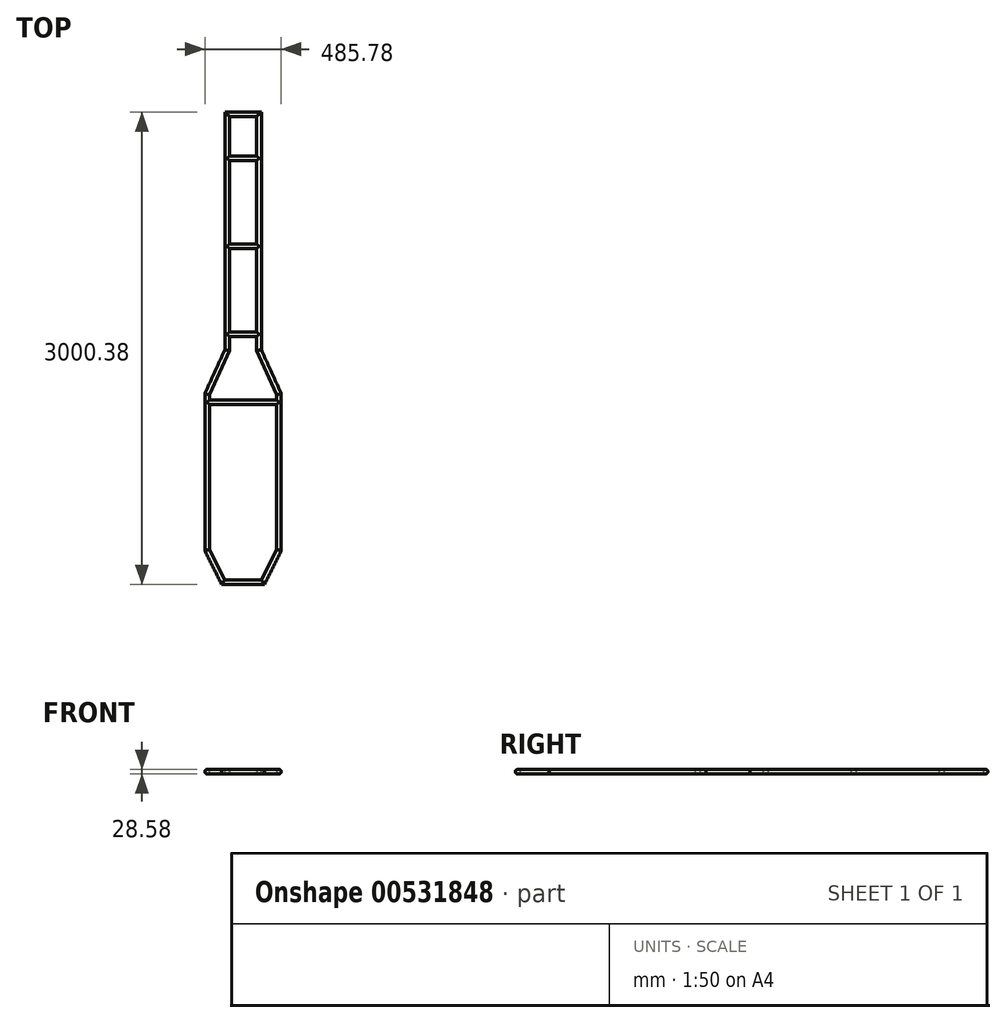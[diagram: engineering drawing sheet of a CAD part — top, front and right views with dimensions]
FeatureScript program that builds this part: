
annotation { "Feature Type Name" : "Feature", "Feature Type Description" : "" }
export const myFeature = defineFeature(function(context is Context, id is Id, definition is map)
    precondition{}
    {
        {
            var Q0;
            Q0=qCreatedBy(makeId("Top.planeOp"),FACE);
            var sketch = newSketch(context, id + "F0", { "sketchPlane" : qUnion([Q0])});
            skLineSegment(sketch, "E0", {"start": v(-228.6, 495.3) * mm, "end": v(-228.6, -495.3) * mm});
            skLineSegment(sketch, "E1", {"start": v(228.6, 495.3) * mm, "end": v(228.6, -495.3) * mm});
            skLineSegment(sketch, "E2", {"start": v(-228.6, 0) * mm, "end": v(228.6, 0) * mm, "construction": true});
            skLineSegment(sketch, "E3", {"start": v(-228.6, 292.1) * mm, "end": v(228.6, 101.6) * mm, "construction": true});
            skLineSegment(sketch, "E4", {"start": v(228.6, 292.1) * mm, "end": v(-228.6, 101.6) * mm, "construction": true});
            skLineSegment(sketch, "E5", {"start": v(-228.6, -292.1) * mm, "end": v(228.6, -101.6) * mm, "construction": true});
            skLineSegment(sketch, "E6", {"start": v(228.6, -292.1) * mm, "end": v(-228.6, -101.6) * mm, "construction": true});
            skLineSegment(sketch, "E7", {"start": v(0, 2273.3) * mm, "end": v(0, -698.5) * mm, "construction": true});
            skLineSegment(sketch, "E8", {"start": v(-228.6, 495.3) * mm, "end": v(-101.6, 774.7) * mm});
            skLineSegment(sketch, "E9", {"start": v(-101.6, 774.7) * mm, "end": v(-101.6, 2273.3) * mm});
            skLineSegment(sketch, "E10", {"start": v(-101.6, 2273.3) * mm, "end": v(101.6, 2273.3) * mm});
            skLineSegment(sketch, "E11", {"start": v(101.6, 2273.3) * mm, "end": v(101.6, 774.7) * mm});
            skLineSegment(sketch, "E12", {"start": v(101.6, 774.7) * mm, "end": v(228.6, 495.3) * mm});
            skPoint(sketch, "E13", {"position": v(0, 2273.3) * mm});
            skLineSegment(sketch, "E14", {"start": v(-127, -698.5) * mm, "end": v(127, -698.5) * mm});
            skLineSegment(sketch, "E15", {"start": v(127, -698.5) * mm, "end": v(228.6, -495.3) * mm});
            skLineSegment(sketch, "E16", {"start": v(-228.6, -495.3) * mm, "end": v(-127, -698.5) * mm});
            skLineSegment(sketch, "E17", {"start": v(-101.6, 1993.9) * mm, "end": v(101.6, 1993.9) * mm});
            skLineSegment(sketch, "E18", {"start": v(-101.6, 876.3) * mm, "end": v(101.6, 876.3) * mm});
            skLineSegment(sketch, "E19", {"start": v(-101.6, 1435.1) * mm, "end": v(101.6, 1435.1) * mm});
            skLineSegment(sketch, "E20", {"start": v(228.6, 444.5) * mm, "end": v(-228.6, 444.5) * mm});
            skLineSegment(sketch, "E21", {"start": v(228.6, -393.7) * mm, "end": v(-228.6, -393.7) * mm});
            skSolve(sketch);
        }
        {
            var Q0;
            Q0=qCreatedBy(makeId("Front.planeOp"),FACE);
            var sketch = newSketch(context, id + "F1", { "sketchPlane" : qUnion([Q0])});
            skCircle(sketch, "E22", {"center": v(228.6, 0) * mm, "radius": 14.29 * mm});
            skSolve(sketch);
        }
        {
            var Q0;
            Q0=makeQuery(id+"F1.imprint","IMPRINT",FACE,{"disambiguationData":[TD([[makeQuery(id+"F1.imprint","IMPRINT",EDGE,{"derivedFrom":sQuery(id+"F1.wireOp",EDGE,"E22")}),1.0]])]});
            var Q1;
            Q1=sQuery(id+"F0.wireOp",EDGE,"E1");
            var Q2;
            Q2=sQuery(id+"F0.wireOp",EDGE,"E12");
            var Q3;
            Q3=sQuery(id+"F0.wireOp",EDGE,"E11");
            var Q4;
            Q4=sQuery(id+"F0.wireOp",EDGE,"E10");
            var Q5;
            Q5=sQuery(id+"F0.wireOp",EDGE,"E9");
            var Q6;
            Q6=sQuery(id+"F0.wireOp",EDGE,"E8");
            var Q7;
            Q7=sQuery(id+"F0.wireOp",EDGE,"E0");
            var Q8;
            Q8=sQuery(id+"F0.wireOp",EDGE,"E16");
            var Q9;
            Q9=sQuery(id+"F0.wireOp",EDGE,"E14");
            var Q10;
            Q10=sQuery(id+"F0.wireOp",EDGE,"E15");
            sweep(context, id + "F2", {"profiles" : qUnion([Q0]), "path" : qUnion([Q1, Q2, Q3, Q4, Q5, Q6, Q7, Q8, Q9, Q10])});
        }
        {
            var Q0;
            Q0=qCreatedBy(makeId("Right.planeOp"),FACE);
            var sketch = newSketch(context, id + "F3", { "sketchPlane" : qUnion([Q0])});
            skCircle(sketch, "E23", {"center": v(444.5, 0) * mm, "radius": 14.29 * mm});
            skCircle(sketch, "E24", {"center": v(876.3, 0) * mm, "radius": 14.29 * mm});
            skCircle(sketch, "E25", {"center": v(1435.1, 0) * mm, "radius": 14.29 * mm});
            skCircle(sketch, "E26", {"center": v(1993.9, 0) * mm, "radius": 14.29 * mm});
            skSolve(sketch);
        }
        {
            var Q0;
            Q0 = qSketchRegion(id + "F3", true);
            extrude(context, id + "F4", {"entities" : qUnion([Q0]), "operationType" : NewBodyOperationType.ADD, "endBound" : BoundingType.UP_TO_NEXT, "depth" : 25.4 * mm, "offsetDistance" : 25.4 * mm, "hasSecondDirection" : true, "secondDirectionBound" : SecondDirectionBoundingType.UP_TO_NEXT, "secondDirectionOppositeDirection" : true, "secondDirectionDepth" : 25.4 * mm});
        }
    });
